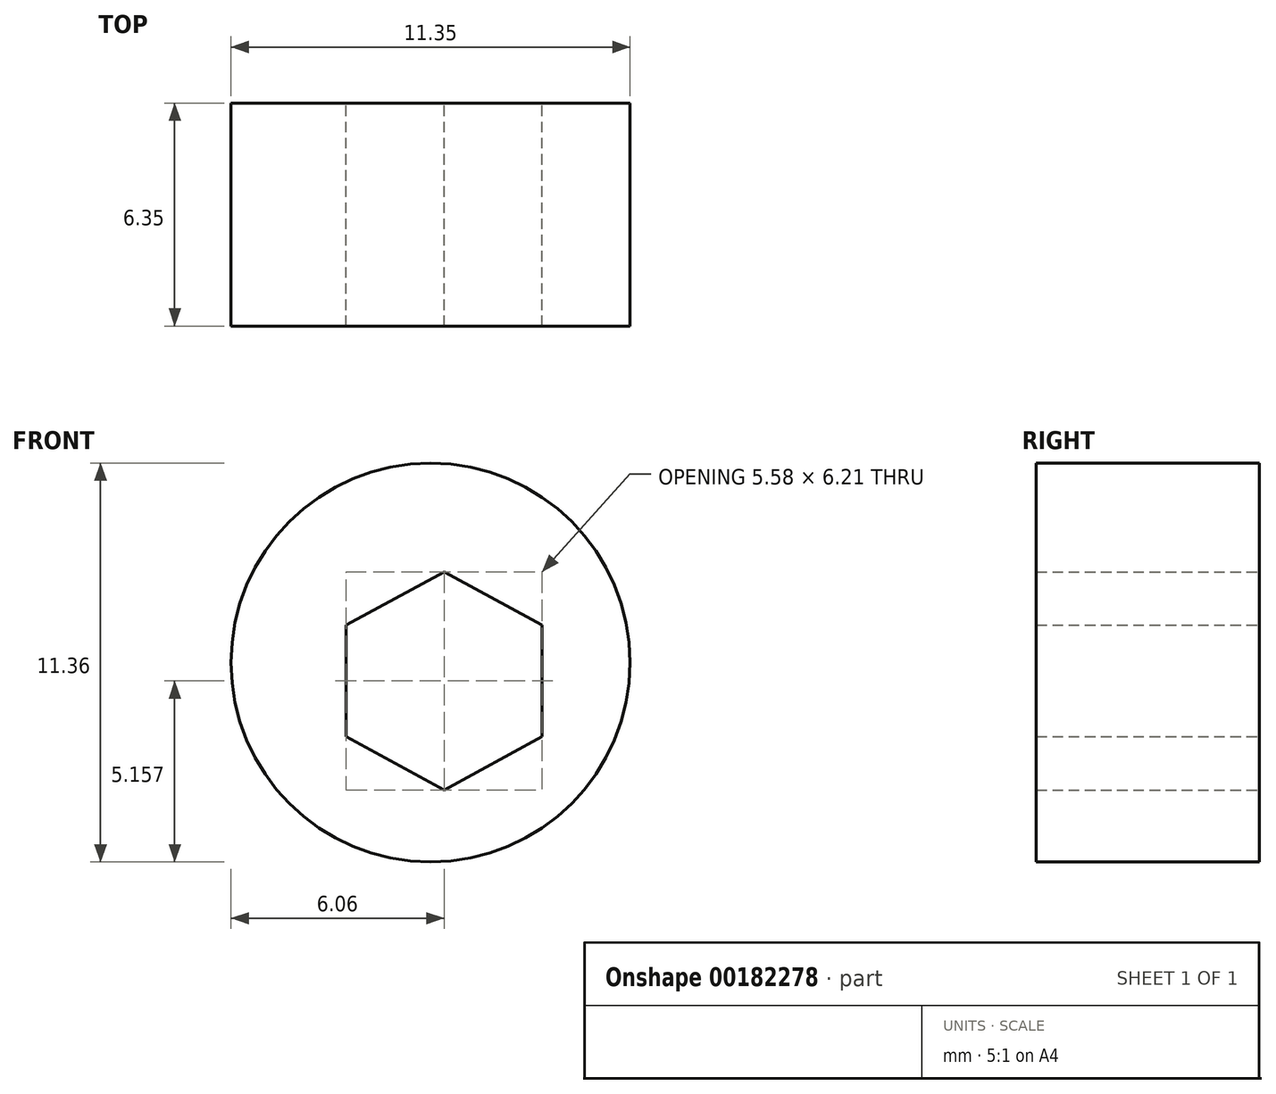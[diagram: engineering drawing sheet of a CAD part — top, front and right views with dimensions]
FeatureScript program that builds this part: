
annotation { "Feature Type Name" : "Feature", "Feature Type Description" : "" }
export const myFeature = defineFeature(function(context is Context, id is Id, definition is map)
    precondition{}
    {
        {
            var Q0;
            Q0=qCreatedBy(makeId("Front.planeOp"),FACE);
            var sketch = newSketch(context, id + "F0", { "sketchPlane" : qUnion([Q0])});
            skCircle(sketch, "E0", {"center": v(-3.17, 2.1) * mm, "radius": 5.68 * mm});
            skLineSegment(sketch, "E1", {"start": v(-5.58, 3.17) * mm, "end": v(-2.79, 4.7) * mm});
            skLineSegment(sketch, "E2", {"start": v(-2.79, 4.7) * mm, "end": v(0, 3.18) * mm});
            skLineSegment(sketch, "E3", {"start": v(-5.58, 3.18) * mm, "end": v(-5.58, 0) * mm});
            skLineSegment(sketch, "E4", {"start": v(-5.58, 0) * mm, "end": v(-2.79, -1.52) * mm});
            skLineSegment(sketch, "E5", {"start": v(-2.79, -1.52) * mm, "end": v(0, 0) * mm});
            skLineSegment(sketch, "E6", {"start": v(0, 0) * mm, "end": v(0, 3.18) * mm});
            skSolve(sketch);
        }
        {
            var Q0;
            Q0=makeQuery(id+"F0.imprint","IMPRINT",FACE,{"disambiguationData":[TD([[makeQuery(id+"F0.imprint","IMPRINT",EDGE,{"derivedFrom":sQuery(id+"F0.wireOp",EDGE,"E0")}),1.0]])]});
            extrude(context, id + "F1", {"entities" : qUnion([Q0]), "depth" : 6.35 * mm});
        }
    });
